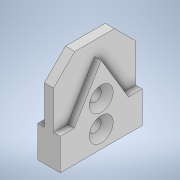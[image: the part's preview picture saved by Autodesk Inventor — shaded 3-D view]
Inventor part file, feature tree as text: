
AUTODESK INVENTOR PART (.ipt)
format: ipt  version: 2022 (Build 260153000, 153)  size: 192,512 bytes
history: native  units: in
note: dims shown in document units (in); Inventor stores cm internally (conversion verified against a paired STEP export)
features: sketch x5, extrude x4, mirror x3, other x3, hole x2, projected_geometry x2, chamfer x1
ambient origin geometry x8: Origin, YZ Plane, XZ Plane, XY Plane, X Axis, Y Axis, Z Axis, Center Point
bodies: Solid1 (feature_tree)
feature tree (20):
  extrude  "Extrusion1"  Depth=0.8858in
  extrude  "Extrusion4"  Depth=0.1378in
  mirror  "Mirror2"
  extrude  "Extrusion5"  Depth=0.0984in TaperAngle=0.0deg
  extrude  "Extrusion6"  Depth=0.3937in TaperAngle=0.0deg
  mirror  "Mirror3"
  mirror  "Mirror4"
  sketch  "Sketch9"  dims[d40=0.1575in d63=0.3937in d64=0.3937in d43=0.1772in d44=0.2362in d45=0.3543in d46=0.0787in d47=90.0deg d48=0.315in d49=0.8108in d50=0.3937in d65=0.3937in d66=0.3937in d53=0.1772in d54=0.2362in d55=0.3543in d56=0.0787in d57=90.0deg d58=0.315in d59=0.8108in d60=0.315in d61=0.0787in d62=45.0deg d67=0.0197in d68=0.0344in d69=0.0197in d70=0.0344in]
  other  "Work Point4"
  other  "Work Point5"
  hole  "Hole3"  [1 undecoded]
  other  "Work Point6"
  hole  "Hole4"  [1 undecoded]
  chamfer  "Chamfer1"  Distance=0.0197in
  sketch  "Sketch1"  dims[d0=1.2205in d1=0.8858in]
  sketch  "Sketch2"  dims[d2=0.1378in d3=0.0in d31=0.8067in]
  sketch  "Sketch7"  dims[d33=0.6723in d34=0.0984in d35=0.0in]
  projected_geometry  "Projected Loop2"
  sketch  "Sketch8"  dims[d36=0.4724in d37=0.0in d38=0.3937in d39=0.0in]
  projected_geometry  "Projected Loop3"
note: 2 required parameter values undecoded (feature->parameter linkage not recoverable at this tier; creation-order binding heuristic only, values carry confidence <= 0.55)
